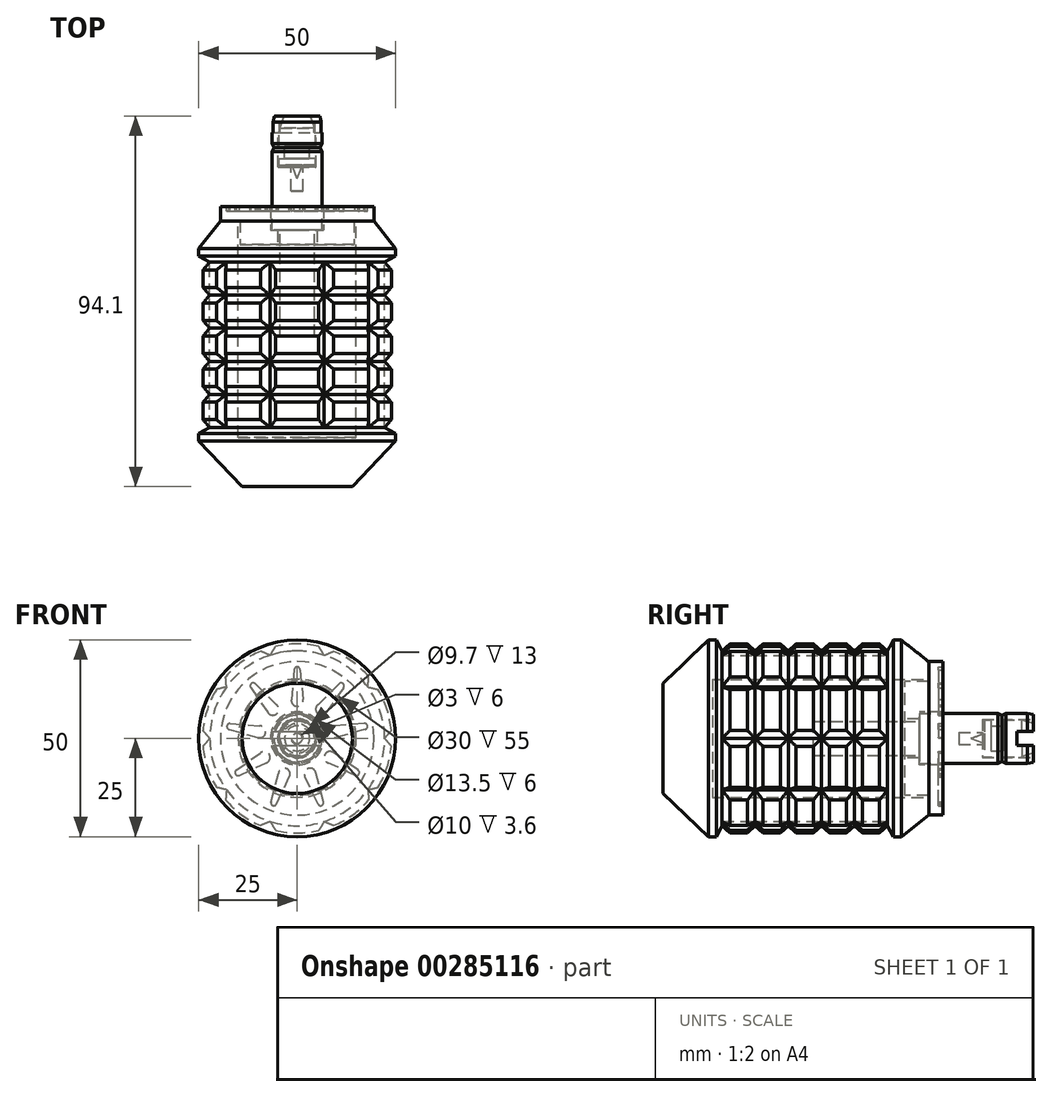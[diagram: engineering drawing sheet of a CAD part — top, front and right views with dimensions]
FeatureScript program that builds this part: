
annotation { "Feature Type Name" : "Feature", "Feature Type Description" : "" }
export const myFeature = defineFeature(function(context is Context, id is Id, definition is map)
    precondition{}
    {
        {
            var Q0;
            Q0=qCreatedBy(makeId("Front.planeOp"),FACE);
            var sketch = newSketch(context, id + "F0", { "sketchPlane" : qUnion([Q0])});
            skArc(sketch, "E0", {"start": v(-9.3, 22.13) * mm, "mid": v(-14.1, 19.42) * mm, "end": v(-18.17, 15.67) * mm});
            skLineSegment(sketch, "E1", {"start": v(-9.3, 22.13) * mm, "end": v(-6.86, 21.11) * mm});
            skLineSegment(sketch, "E2", {"start": v(-5.5, 23.36) * mm, "end": v(-6.86, 21.11) * mm});
            skLineSegment(sketch, "E3.1.0", {"start": v(-18.17, 15.67) * mm, "end": v(-17.96, 13.05) * mm});
            skLineSegment(sketch, "E3.1.1", {"start": v(-20.52, 12.44) * mm, "end": v(-17.96, 13.05) * mm});
            skLineSegment(sketch, "E3.2.0", {"start": v(-23.92, 2) * mm, "end": v(-22.2, 0) * mm});
            skLineSegment(sketch, "E3.2.1", {"start": v(-23.92, -2) * mm, "end": v(-22.2, 0) * mm});
            skLineSegment(sketch, "E3.3.0", {"start": v(-20.52, -12.44) * mm, "end": v(-17.96, -13.05) * mm});
            skLineSegment(sketch, "E3.3.1", {"start": v(-18.17, -15.67) * mm, "end": v(-17.96, -13.05) * mm});
            skLineSegment(sketch, "E3.4.0", {"start": v(-9.3, -22.13) * mm, "end": v(-6.86, -21.11) * mm});
            skLineSegment(sketch, "E3.4.1", {"start": v(-5.5, -23.36) * mm, "end": v(-6.86, -21.11) * mm});
            skLineSegment(sketch, "E3.5.0", {"start": v(5.5, -23.36) * mm, "end": v(6.86, -21.11) * mm});
            skLineSegment(sketch, "E3.5.1", {"start": v(9.3, -22.13) * mm, "end": v(6.86, -21.11) * mm});
            skLineSegment(sketch, "E3.6.0", {"start": v(18.17, -15.67) * mm, "end": v(17.96, -13.05) * mm});
            skLineSegment(sketch, "E3.6.1", {"start": v(20.52, -12.44) * mm, "end": v(17.96, -13.05) * mm});
            skLineSegment(sketch, "E3.7.0", {"start": v(23.92, -2) * mm, "end": v(22.2, 0) * mm});
            skLineSegment(sketch, "E3.7.1", {"start": v(23.92, 2) * mm, "end": v(22.2, 0) * mm});
            skLineSegment(sketch, "E3.8.0", {"start": v(20.52, 12.44) * mm, "end": v(17.96, 13.05) * mm});
            skLineSegment(sketch, "E3.8.1", {"start": v(18.17, 15.67) * mm, "end": v(17.96, 13.05) * mm});
            skLineSegment(sketch, "E3.9.0", {"start": v(9.3, 22.13) * mm, "end": v(6.86, 21.11) * mm});
            skLineSegment(sketch, "E3.9.1", {"start": v(5.5, 23.36) * mm, "end": v(6.86, 21.11) * mm});
            skArc(sketch, "E4.trimOffspring", {"start": v(-20.52, 12.44) * mm, "mid": v(-22.83, 7.42) * mm, "end": v(-23.92, 2) * mm});
            skArc(sketch, "E5.trimOffspring", {"start": v(-23.92, -2) * mm, "mid": v(-22.83, -7.42) * mm, "end": v(-20.52, -12.44) * mm});
            skArc(sketch, "E6.trimOffspring", {"start": v(-18.17, -15.67) * mm, "mid": v(-14.1, -19.42) * mm, "end": v(-9.3, -22.13) * mm});
            skArc(sketch, "E7.trimOffspring", {"start": v(23.92, 2) * mm, "mid": v(22.83, 7.42) * mm, "end": v(20.52, 12.44) * mm});
            skArc(sketch, "E8.trimOffspring", {"start": v(20.52, -12.44) * mm, "mid": v(22.83, -7.42) * mm, "end": v(23.92, -2) * mm});
            skArc(sketch, "E9.trimOffspring", {"start": v(9.3, -22.13) * mm, "mid": v(14.1, -19.42) * mm, "end": v(18.17, -15.67) * mm});
            skArc(sketch, "E10.trimOffspring", {"start": v(-5.5, -23.36) * mm, "mid": v(0, -24) * mm, "end": v(5.5, -23.36) * mm});
            skArc(sketch, "E11.trimOffspring", {"start": v(18.17, 15.67) * mm, "mid": v(14.1, 19.42) * mm, "end": v(9.3, 22.13) * mm});
            skArc(sketch, "E12.trimOffspring", {"start": v(5.5, 23.36) * mm, "mid": v(0, 24) * mm, "end": v(-5.5, 23.36) * mm});
            skSolve(sketch);
        }
        {
            var Q0;
            Q0 = qSketchRegion(id + "F0", true);
            extrude(context, id + "F1", {"entities" : qUnion([Q0]), "endBound" : BoundingType.SYMMETRIC, "depth" : 42 * mm});
        }
        {
            var Q0;
            Q0=qCreatedBy(makeId("Right.planeOp"),FACE);
            var sketch = newSketch(context, id + "F2", { "sketchPlane" : qUnion([Q0])});
            skLineSegment(sketch, "E13.0", {"start": v(21, 23.36) * mm, "end": v(21, 24) * mm, "construction": true});
            skLineSegment(sketch, "E14.0", {"start": v(21, 23.36) * mm, "end": v(21, 21.11) * mm, "construction": true});
            skLineSegment(sketch, "E15", {"start": v(0, 0) * mm, "end": v(0, 30.64) * mm, "construction": true});
            skLineSegment(sketch, "E16", {"start": v(21, 24.46) * mm, "end": v(21, 27.24) * mm, "construction": true});
            skLineSegment(sketch, "E17", {"start": v(21, 27.24) * mm, "end": v(-21, 27.24) * mm, "construction": true});
            skLineSegment(sketch, "E18", {"start": v(-21, 27.24) * mm, "end": v(-21, 24) * mm, "construction": true});
            skPoint(sketch, "E19.0.end.orphan", {"position": v(-21, 21.11) * mm});
            skLineSegment(sketch, "E20", {"start": v(-21, 24) * mm, "end": v(-21, 22.2) * mm});
            skPoint(sketch, "E21.end.orphan", {"position": v(21, 24) * mm});
            skLineSegment(sketch, "E22", {"start": v(-19, 24) * mm, "end": v(-21, 22.2) * mm});
            skLineSegment(sketch, "E23", {"start": v(-21, 27.24) * mm, "end": v(-12.6, 27.24) * mm});
            skLineSegment(sketch, "E24", {"start": v(-12.6, 27.24) * mm, "end": v(-4.2, 27.24) * mm});
            skLineSegment(sketch, "E25", {"start": v(-4.2, 27.24) * mm, "end": v(4.2, 27.24) * mm});
            skLineSegment(sketch, "E26", {"start": v(4.2, 27.24) * mm, "end": v(12.6, 27.24) * mm});
            skLineSegment(sketch, "E27", {"start": v(12.6, 27.24) * mm, "end": v(21, 27.24) * mm});
            skLineSegment(sketch, "E28", {"start": v(-12.6, 27.24) * mm, "end": v(-12.6, 10.8) * mm, "construction": true});
            skLineSegment(sketch, "E29", {"start": v(-4.2, 27.24) * mm, "end": v(-4.2, 11.63) * mm, "construction": true});
            skLineSegment(sketch, "E30", {"start": v(4.2, 27.24) * mm, "end": v(4.2, 11.59) * mm, "construction": true});
            skLineSegment(sketch, "E31", {"start": v(12.6, 27.24) * mm, "end": v(12.6, 11.39) * mm, "construction": true});
            skLineSegment(sketch, "E32", {"start": v(-19, 24) * mm, "end": v(-14.6, 24) * mm});
            skPoint(sketch, "E33", {"position": v(-12.6, 24) * mm});
            skPoint(sketch, "E34", {"position": v(-4.2, 24) * mm});
            skPoint(sketch, "E35", {"position": v(4.2, 24) * mm});
            skPoint(sketch, "E36", {"position": v(12.6, 24) * mm});
            skLineSegment(sketch, "E37", {"start": v(-12.6, 22.2) * mm, "end": v(-14.6, 24) * mm});
            skLineSegment(sketch, "E38", {"start": v(-10.6, 24) * mm, "end": v(-12.6, 22.2) * mm});
            skLineSegment(sketch, "E39", {"start": v(-6.2, 24) * mm, "end": v(-4.2, 22.2) * mm});
            skLineSegment(sketch, "E40", {"start": v(-4.2, 22.2) * mm, "end": v(-2.2, 24) * mm});
            skLineSegment(sketch, "E41", {"start": v(2.2, 24) * mm, "end": v(4.2, 22.2) * mm});
            skLineSegment(sketch, "E42", {"start": v(4.2, 22.2) * mm, "end": v(6.2, 24) * mm});
            skLineSegment(sketch, "E43", {"start": v(10.6, 24) * mm, "end": v(12.6, 22.2) * mm});
            skLineSegment(sketch, "E44", {"start": v(12.6, 22.2) * mm, "end": v(14.6, 24) * mm});
            skLineSegment(sketch, "E45", {"start": v(21, 22.2) * mm, "end": v(19, 24) * mm});
            skLineSegment(sketch, "E46", {"start": v(-21, 27.24) * mm, "end": v(-21, 22.2) * mm});
            skLineSegment(sketch, "E47", {"start": v(21, 27.24) * mm, "end": v(21, 22.2) * mm});
            skLineSegment(sketch, "E48.trimOffspring", {"start": v(-10.6, 24) * mm, "end": v(-6.2, 24) * mm});
            skLineSegment(sketch, "E49.trimOffspring", {"start": v(-2.2, 24) * mm, "end": v(2.2, 24) * mm});
            skLineSegment(sketch, "E50.trimOffspring", {"start": v(6.2, 24) * mm, "end": v(10.6, 24) * mm});
            skLineSegment(sketch, "E51.trimOffspring", {"start": v(14.6, 24) * mm, "end": v(19, 24) * mm});
            skLineSegment(sketch, "E52", {"start": v(0, 0) * mm, "end": v(61.19, 0) * mm, "construction": true});
            skLineSegment(sketch, "E53", {"start": v(0, 0) * mm, "end": v(-52.13, 0) * mm, "construction": true});
            skSolve(sketch);
        }
        {
            var Q0;
            Q0 = qSketchRegion(id + "F2", true);
            var Q1;
            Q1=sQuery(id+"F2.wireOp",EDGE,"E52");
            revolve(context, id + "F3", {"operationType" : NewBodyOperationType.REMOVE, "entities" : qUnion([Q0]), "axis" : qUnion([Q1]), "revolveType" : RevolveType.FULL, "oppositeDirection" : true});
        }
        {
            var Q0;
            Q0=qCreatedBy(makeId("Top.planeOp"),FACE);
            var sketch = newSketch(context, id + "F4", { "sketchPlane" : qUnion([Q0])});
            skLineSegment(sketch, "E54", {"start": v(0, 0) * mm, "end": v(0, 21) * mm, "construction": true});
            skLineSegment(sketch, "E55", {"start": v(0, 0) * mm, "end": v(0, -40.18) * mm, "construction": true});
            skPoint(sketch, "E56.0", {"position": v(-22.2, 21) * mm});
            skPoint(sketch, "E57", {"position": v(0, 21) * mm});
            skPoint(sketch, "E58.orphan", {"position": v(6.86, 21) * mm});
            skPoint(sketch, "E59.trimOffspring.end.orphan", {"position": v(22.2, 21) * mm});
            skPoint(sketch, "E59.trimOffspring.start.orphan", {"position": v(17.96, 21) * mm});
            skLineSegment(sketch, "E60", {"start": v(-25, 24.5) * mm, "end": v(-25, 22.5) * mm});
            skLineSegment(sketch, "E61", {"start": v(-19.5, 31.5) * mm, "end": v(-25, 24.5) * mm});
            skLineSegment(sketch, "E62", {"start": v(-25, 24.5) * mm, "end": v(-25, 22.5) * mm, "construction": true});
            skLineSegment(sketch, "E63", {"start": v(-25, 22.5) * mm, "end": v(-22.2, 21) * mm});
            skPoint(sketch, "E64.0.start.orphan", {"position": v(-17.96, 21) * mm});
            skPoint(sketch, "E65.0.start.orphan", {"position": v(-6.86, 21) * mm});
            skLineSegment(sketch, "E66.trimOffspring", {"start": v(0, 31.5) * mm, "end": v(0, 57.57) * mm, "construction": true});
            skLineSegment(sketch, "E67", {"start": v(0, 31.5) * mm, "end": v(-19.5, 31.5) * mm});
            skLineSegment(sketch, "E68", {"start": v(0, 31.5) * mm, "end": v(0, 21) * mm});
            skLineSegment(sketch, "E69", {"start": v(-22.2, 21) * mm, "end": v(0, 21) * mm});
            skLineSegment(sketch, "E70", {"start": v(0, 35.81) * mm, "end": v(0, 0) * mm, "construction": true});
            skLineSegment(sketch, "E71.MirrorCS", {"start": v(-25, -22.5) * mm, "end": v(-22.2, -21) * mm});
            skLineSegment(sketch, "E72.MirrorCS", {"start": v(-22.2, -21) * mm, "end": v(0, -21) * mm});
            skLineSegment(sketch, "E73", {"start": v(0, -21) * mm, "end": v(0, -36) * mm});
            skLineSegment(sketch, "E74", {"start": v(0, -36) * mm, "end": v(-14, -36) * mm});
            skPoint(sketch, "E75.MirrorCS.end.orphan", {"position": v(-25, -22.5) * mm});
            skPoint(sketch, "E75.MirrorCS.start.orphan", {"position": v(-25, -24.5) * mm});
            skLineSegment(sketch, "E76", {"start": v(-25, -22.5) * mm, "end": v(-25, -24.5) * mm});
            skPoint(sketch, "E77.MirrorCS.start.orphan", {"position": v(0, -31.5) * mm});
            skLineSegment(sketch, "E78", {"start": v(-25, -24.5) * mm, "end": v(-14, -36) * mm});
            skSolve(sketch);
        }
        {
            var Q0;
            Q0 = qSketchRegion(id + "F4", true);
            var Q1;
            Q1=sQuery(id+"F4.wireOp",EDGE,"E68");
            revolve(context, id + "F5", {"operationType" : NewBodyOperationType.ADD, "entities" : qUnion([Q0]), "axis" : qUnion([Q1]), "revolveType" : RevolveType.FULL});
        }
        {
            var Q0;
            Q0=makeQuery(id+"F5.opRevolve","SWEPT_FACE",FACE,{"disambiguationData":[OSD([sQuery(id+"F4.wireOp",EDGE,"E67")])]});
            cPlane(context, id + "F6", {"entities" : qUnion([Q0]), "cplaneType" : CPlaneType.OFFSET, "offset" : 0 * mm, "width" : 150 * mm, "height" : 150 * mm});
        }
        {
            var Q0;
            Q0=qCreatedBy(id+"F6.planeOp",FACE);
            var sketch = newSketch(context, id + "F7", { "sketchPlane" : qUnion([Q0])});
            skCircle(sketch, "E79", {"center": v(0, 0) * mm, "radius": 15 * mm});
            skSolve(sketch);
        }
        {
            var Q0;
            Q0 = qSketchRegion(id + "F7", true);
            extrude(context, id + "F8", {"entities" : qUnion([Q0]), "operationType" : NewBodyOperationType.REMOVE, "oppositeDirection" : true, "depth" : 55 * mm});
        }
        {
            var Q0;
            Q0=qCreatedBy(makeId("Top.planeOp"),FACE);
            var sketch = newSketch(context, id + "F9", { "sketchPlane" : qUnion([Q0])});
            skLineSegment(sketch, "E80", {"start": v(0, 0) * mm, "end": v(0, 31.5) * mm, "construction": true});
            skLineSegment(sketch, "E81.0", {"start": v(-15, 31.5) * mm, "end": v(0, 31.5) * mm, "construction": true});
            skLineSegment(sketch, "E82.0", {"start": v(-19.5, 31.5) * mm, "end": v(0, 31.5) * mm, "construction": true});
            skPoint(sketch, "E83", {"position": v(0, 31.5) * mm});
            skLineSegment(sketch, "E84", {"start": v(14.5, 31.5) * mm, "end": v(14.5, 25.5) * mm});
            skLineSegment(sketch, "E85.trimOffspring", {"start": v(14.5, 31.5) * mm, "end": v(19.5, 31.5) * mm, "construction": true});
            skLineSegment(sketch, "E86.trimOffspring", {"start": v(14.5, 31.5) * mm, "end": v(15, 31.5) * mm, "construction": true});
            skLineSegment(sketch, "E87", {"start": v(5, 25.5) * mm, "end": v(14.5, 25.5) * mm});
            skLineSegment(sketch, "E88", {"start": v(19.5, 31.5) * mm, "end": v(19.5, 35.1) * mm});
            skLineSegment(sketch, "E89", {"start": v(19.5, 35.1) * mm, "end": v(6.75, 35.1) * mm});
            skLineSegment(sketch, "E90", {"start": v(0, 31.5) * mm, "end": v(0, 25.5) * mm});
            skLineSegment(sketch, "E91", {"start": v(14.5, 31.5) * mm, "end": v(19.5, 31.5) * mm});
            skLineSegment(sketch, "E92", {"start": v(6.75, 35.1) * mm, "end": v(6.75, 29.1) * mm});
            skLineSegment(sketch, "E93", {"start": v(6.75, 29.1) * mm, "end": v(5, 29.1) * mm});
            skLineSegment(sketch, "E94", {"start": v(5, 25.5) * mm, "end": v(5, 29.1) * mm});
            skLineSegment(sketch, "E95.trimOffspring", {"start": v(0, 35.1) * mm, "end": v(0, 71.87) * mm, "construction": true});
            skSolve(sketch);
        }
        {
            var Q0;
            Q0 = qSketchRegion(id + "F9", true);
            var Q1;
            Q1=sQuery(id+"F9.wireOp",EDGE,"E95.trimOffspring");
            revolve(context, id + "F10", {"entities" : qUnion([Q0]), "axis" : qUnion([Q1]), "revolveType" : RevolveType.FULL});
        }
        {
            var Q0;
            Q0=makeQuery(id+"F10.opRevolve","SWEPT_FACE",FACE,{"disambiguationData":[OSD([sQuery(id+"F9.wireOp",EDGE,"E89")])]});
            cPlane(context, id + "F11", {"entities" : qUnion([Q0]), "cplaneType" : CPlaneType.OFFSET, "offset" : 0 * mm, "width" : 150 * mm, "height" : 150 * mm});
        }
        {
            var Q0;
            Q0=qCreatedBy(id+"F11.planeOp",FACE);
            var sketch = newSketch(context, id + "F12", { "sketchPlane" : qUnion([Q0])});
            skCircle(sketch, "E96.0.0", {"center": v(0, 0) * mm, "radius": 19.5 * mm, "construction": true});
            skLineSegment(sketch, "E97", {"start": v(-32.31, 0) * mm, "end": v(39.47, 0) * mm, "construction": true});
            skLineSegment(sketch, "E98", {"start": v(0, 28.13) * mm, "end": v(0, 18.15) * mm, "construction": true});
            skPoint(sketch, "E99", {"position": v(0, 8.15) * mm});
            skArc(sketch, "E100", {"start": v(-1.47, 9.94) * mm, "mid": v(0, 8.15) * mm, "end": v(1.47, 9.94) * mm});
            skArc(sketch, "E101", {"start": v(0.75, 17.4) * mm, "mid": v(0, 18.15) * mm, "end": v(-0.75, 17.4) * mm});
            skLineSegment(sketch, "E102", {"start": v(-0.75, 17.4) * mm, "end": v(-1.5, 9.65) * mm});
            skLineSegment(sketch, "E103", {"start": v(0.75, 17.4) * mm, "end": v(1.5, 9.65) * mm});
            skLineSegment(sketch, "E104.trimOffspring", {"start": v(0, 8.15) * mm, "end": v(0, -29.51) * mm, "construction": true});
            skArc(sketch, "E105.1.0", {"start": v(11.76, 12.85) * mm, "mid": v(11.67, 13.9) * mm, "end": v(10.6, 13.81) * mm});
            skLineSegment(sketch, "E105.1.1", {"start": v(11.76, 12.85) * mm, "end": v(7.35, 6.43) * mm});
            skArc(sketch, "E105.1.2", {"start": v(5.26, 8.56) * mm, "mid": v(5.24, 6.24) * mm, "end": v(7.52, 6.67) * mm});
            skLineSegment(sketch, "E105.1.3", {"start": v(10.6, 13.81) * mm, "end": v(5.05, 8.36) * mm});
            skArc(sketch, "E105.2.0", {"start": v(17.27, 2.28) * mm, "mid": v(17.87, 3.15) * mm, "end": v(17, 3.76) * mm});
            skLineSegment(sketch, "E105.2.1", {"start": v(17.27, 2.28) * mm, "end": v(9.76, 0.2) * mm});
            skArc(sketch, "E105.2.2", {"start": v(9.53, 3.18) * mm, "mid": v(8.03, 1.42) * mm, "end": v(10.04, 0.28) * mm});
            skLineSegment(sketch, "E105.2.3", {"start": v(17, 3.76) * mm, "end": v(9.24, 3.15) * mm});
            skArc(sketch, "E105.3.0", {"start": v(14.7, -9.35) * mm, "mid": v(15.72, -9.08) * mm, "end": v(15.44, -8.05) * mm});
            skLineSegment(sketch, "E105.3.1", {"start": v(14.7, -9.35) * mm, "end": v(7.6, -6.12) * mm});
            skArc(sketch, "E105.3.2", {"start": v(9.34, -3.7) * mm, "mid": v(7.06, -4.08) * mm, "end": v(7.87, -6.24) * mm});
            skLineSegment(sketch, "E105.3.3", {"start": v(15.44, -8.05) * mm, "end": v(9.1, -3.53) * mm});
            skArc(sketch, "E105.4.0", {"start": v(5.25, -16.6) * mm, "mid": v(6.2, -17.06) * mm, "end": v(6.66, -16.1) * mm});
            skLineSegment(sketch, "E105.4.1", {"start": v(5.25, -16.6) * mm, "end": v(1.9, -9.58) * mm});
            skArc(sketch, "E105.4.2", {"start": v(4.78, -8.83) * mm, "mid": v(2.79, -7.66) * mm, "end": v(2.02, -9.84) * mm});
            skLineSegment(sketch, "E105.4.3", {"start": v(6.66, -16.1) * mm, "end": v(4.71, -8.56) * mm});
            skArc(sketch, "E105.5.0", {"start": v(-6.66, -16.1) * mm, "mid": v(-6.2, -17.06) * mm, "end": v(-5.25, -16.6) * mm});
            skLineSegment(sketch, "E105.5.1", {"start": v(-6.66, -16.1) * mm, "end": v(-4.71, -8.56) * mm});
            skArc(sketch, "E105.5.2", {"start": v(-2.02, -9.84) * mm, "mid": v(-2.79, -7.66) * mm, "end": v(-4.78, -8.83) * mm});
            skLineSegment(sketch, "E105.5.3", {"start": v(-5.25, -16.6) * mm, "end": v(-1.9, -9.58) * mm});
            skArc(sketch, "E105.6.0", {"start": v(-15.44, -8.05) * mm, "mid": v(-15.72, -9.07) * mm, "end": v(-14.7, -9.35) * mm});
            skLineSegment(sketch, "E105.6.1", {"start": v(-15.44, -8.05) * mm, "end": v(-9.1, -3.53) * mm});
            skArc(sketch, "E105.6.2", {"start": v(-7.87, -6.24) * mm, "mid": v(-7.06, -4.07) * mm, "end": v(-9.34, -3.7) * mm});
            skLineSegment(sketch, "E105.6.3", {"start": v(-14.7, -9.35) * mm, "end": v(-7.6, -6.12) * mm});
            skArc(sketch, "E105.7.0", {"start": v(-17, 3.76) * mm, "mid": v(-17.87, 3.15) * mm, "end": v(-17.27, 2.28) * mm});
            skLineSegment(sketch, "E105.7.1", {"start": v(-17, 3.76) * mm, "end": v(-9.24, 3.15) * mm});
            skArc(sketch, "E105.7.2", {"start": v(-10.04, 0.28) * mm, "mid": v(-8.03, 1.42) * mm, "end": v(-9.53, 3.18) * mm});
            skLineSegment(sketch, "E105.7.3", {"start": v(-17.27, 2.28) * mm, "end": v(-9.76, 0.2) * mm});
            skArc(sketch, "E105.8.0", {"start": v(-10.6, 13.81) * mm, "mid": v(-11.67, 13.9) * mm, "end": v(-11.76, 12.85) * mm});
            skLineSegment(sketch, "E105.8.1", {"start": v(-10.6, 13.81) * mm, "end": v(-5.05, 8.36) * mm});
            skArc(sketch, "E105.8.2", {"start": v(-7.52, 6.67) * mm, "mid": v(-5.24, 6.24) * mm, "end": v(-5.26, 8.56) * mm});
            skLineSegment(sketch, "E105.8.3", {"start": v(-11.76, 12.85) * mm, "end": v(-7.35, 6.43) * mm});
            skLineSegment(sketch, "E105.anchor1", {"start": v(0, 0) * mm, "end": v(-0.75, 17.4) * mm, "construction": true});
            skLineSegment(sketch, "E105.anchor2", {"start": v(0, 0) * mm, "end": v(-0.75, 17.4) * mm, "construction": true});
            skSolve(sketch);
        }
        {
            var Q0;
            Q0 = qSketchRegion(id + "F12", true);
            extrude(context, id + "F13", {"entities" : qUnion([Q0]), "operationType" : NewBodyOperationType.REMOVE, "oppositeDirection" : true, "depth" : 1.1 * mm});
        }
        {
            var Q0;
            Q0=qCreatedBy(makeId("Right.planeOp"),FACE);
            var sketch = newSketch(context, id + "F14", { "sketchPlane" : qUnion([Q0])});
            skLineSegment(sketch, "E106", {"start": v(59.1, 0) * mm, "end": v(45.1, 0) * mm, "construction": true});
            skLineSegment(sketch, "E107", {"start": v(0, -67.3) * mm, "end": v(0, 60.31) * mm, "construction": true});
            skLineSegment(sketch, "E108.0", {"start": v(29.1, -6.75) * mm, "end": v(29.1, 6.75) * mm, "construction": true});
            skLineSegment(sketch, "E109.0", {"start": v(25.5, -5) * mm, "end": v(25.5, -4.35) * mm, "construction": true});
            skLineSegment(sketch, "E110.0", {"start": v(35.1, -6.75) * mm, "end": v(35.1, 6.75) * mm, "construction": true});
            skLineSegment(sketch, "E111", {"start": v(25.5, -5) * mm, "end": v(29.1, -5) * mm, "construction": true});
            skLineSegment(sketch, "E112", {"start": v(29.1, -6.75) * mm, "end": v(35.1, -6.75) * mm, "construction": true});
            skLineSegment(sketch, "E113", {"start": v(29.1, -6.75) * mm, "end": v(29.1, 0) * mm, "construction": true});
            skLineSegment(sketch, "E114", {"start": v(25.5, -5) * mm, "end": v(25.5, -4.35) * mm});
            skLineSegment(sketch, "E115", {"start": v(35.1, -6.75) * mm, "end": v(35.1, 0) * mm});
            skLineSegment(sketch, "E116", {"start": v(2.1, 0) * mm, "end": v(2.1, -4.35) * mm});
            skLineSegment(sketch, "E117", {"start": v(2.1, -4.35) * mm, "end": v(29.1, -4.35) * mm});
            skLineSegment(sketch, "E118", {"start": v(58.1, 0) * mm, "end": v(58.1, -6.05) * mm});
            skLineSegment(sketch, "E119", {"start": v(56.6, -6.35) * mm, "end": v(51.1, -6.35) * mm});
            skLineSegment(sketch, "E120", {"start": v(29.1, -6.35) * mm, "end": v(29.1, -4.35) * mm});
            skLineSegment(sketch, "E121", {"start": v(58.1, -4.85) * mm, "end": v(45.1, -4.85) * mm});
            skLineSegment(sketch, "E122", {"start": v(45.1, -4.85) * mm, "end": v(45.1, -1.5) * mm});
            skLineSegment(sketch, "E123", {"start": v(39.1, 0) * mm, "end": v(2.1, 0) * mm});
            skLineSegment(sketch, "E124", {"start": v(50.1, -5.87) * mm, "end": v(50.1, -4.85) * mm});
            skLineSegment(sketch, "E125", {"start": v(50.1, -5.87) * mm, "end": v(49.1, -6.35) * mm});
            skLineSegment(sketch, "E126", {"start": v(50.1, -5.87) * mm, "end": v(51.1, -6.35) * mm});
            skLineSegment(sketch, "E127", {"start": v(58.1, -6.05) * mm, "end": v(56.6, -6.35) * mm});
            skPoint(sketch, "E128.orphan", {"position": v(58.1, -6.35) * mm});
            skLineSegment(sketch, "E129.trimOffspring", {"start": v(49.1, -6.35) * mm, "end": v(29.1, -6.35) * mm});
            skPoint(sketch, "E130.orphan", {"position": v(50.1, -6.35) * mm});
            skLineSegment(sketch, "E131.trimOffspring", {"start": v(25.5, 0) * mm, "end": v(25.5, 5) * mm, "construction": true});
            skLineSegment(sketch, "E132", {"start": v(45.1, -1.5) * mm, "end": v(39.1, -1.5) * mm});
            skLineSegment(sketch, "E133", {"start": v(39.1, -1.5) * mm, "end": v(39.1, 0) * mm});
            skLineSegment(sketch, "E134.trimOffspring", {"start": v(39.1, 0) * mm, "end": v(-46.03, 0) * mm, "construction": true});
            skSolve(sketch);
        }
        {
            var Q0;
            Q0 = qSketchRegion(id + "F14", true);
            var Q1;
            Q1=sQuery(id+"F14.wireOp",EDGE,"E106");
            revolve(context, id + "F15", {"entities" : qUnion([Q0]), "axis" : qUnion([Q1]), "revolveType" : RevolveType.FULL});
        }
        {
            var Q0;
            Q0=qCreatedBy(makeId("Right.planeOp"),FACE);
            var sketch = newSketch(context, id + "F16", { "sketchPlane" : qUnion([Q0])});
            skLineSegment(sketch, "E135", {"start": v(58.1, -4.85) * mm, "end": v(45.1, -4.85) * mm, "construction": true});
            skLineSegment(sketch, "E136.0", {"start": v(58.1, 6.05) * mm, "end": v(58.1, 4.85) * mm, "construction": true});
            skLineSegment(sketch, "E137.0", {"start": v(58.1, -4.65) * mm, "end": v(58.1, -4.85) * mm, "construction": true});
            skLineSegment(sketch, "E138.0", {"start": v(45.1, 4.85) * mm, "end": v(45.1, -4.85) * mm, "construction": true});
            skLineSegment(sketch, "E139", {"start": v(45.1, -1.5) * mm, "end": v(39.1, -1.5) * mm, "construction": true});
            skLineSegment(sketch, "E140", {"start": v(39.1, 1.5) * mm, "end": v(45.1, 1.5) * mm, "construction": true});
            skLineSegment(sketch, "E141", {"start": v(68.4, 0) * mm, "end": v(-18.4, 0) * mm, "construction": true});
            skPoint(sketch, "E141.endSnap0", {"position": v(45.1, 0) * mm});
            skPoint(sketch, "E142", {"position": v(58.1, 0) * mm});
            skPoint(sketch, "E143", {"position": v(42.33, 0) * mm});
            skLineSegment(sketch, "E144", {"start": v(45.1, 0) * mm, "end": v(45.6, 0) * mm, "construction": true});
            skLineSegment(sketch, "E145", {"start": v(45.1, -4.85) * mm, "end": v(45.1, -4.65) * mm, "construction": true});
            skLineSegment(sketch, "E146", {"start": v(45.6, -1.28) * mm, "end": v(45.6, -4.65) * mm});
            skLineSegment(sketch, "E147", {"start": v(45.6, -4.65) * mm, "end": v(47.31, -4.65) * mm});
            skPoint(sketch, "E148.orphan", {"position": v(58.1, -6.05) * mm});
            skPoint(sketch, "E149.orphan", {"position": v(58.1, 4.85) * mm});
            skLineSegment(sketch, "E150.trimOffspring", {"start": v(58.1, 0) * mm, "end": v(58.1, -3.75) * mm, "construction": true});
            skLineSegment(sketch, "E151", {"start": v(45.6, -4.65) * mm, "end": v(47.3, -4.65) * mm, "construction": true});
            skLineSegment(sketch, "E152", {"start": v(47.31, -4.67) * mm, "end": v(47.31, -3.17) * mm});
            skLineSegment(sketch, "E153", {"start": v(47.31, -3.17) * mm, "end": v(50.31, -3.17) * mm});
            skLineSegment(sketch, "E154", {"start": v(50.31, -3.17) * mm, "end": v(50.31, -4.65) * mm});
            skLineSegment(sketch, "E155", {"start": v(50.31, -4.65) * mm, "end": v(55.11, -4.65) * mm, "construction": true});
            skLineSegment(sketch, "E156", {"start": v(58.1, -3.75) * mm, "end": v(58.1, -3.05) * mm, "construction": true});
            skLineSegment(sketch, "E157", {"start": v(58.1, -3.75) * mm, "end": v(58.1, -1.75) * mm, "construction": true});
            skLineSegment(sketch, "E158", {"start": v(58.1, -1.75) * mm, "end": v(58.1, -3.75) * mm});
            skLineSegment(sketch, "E159", {"start": v(58.1, -1.75) * mm, "end": v(53.9, -1.75) * mm});
            skLineSegment(sketch, "E160", {"start": v(53.9, -1.75) * mm, "end": v(53.9, 0) * mm});
            skLineSegment(sketch, "E161", {"start": v(53.9, 0) * mm, "end": v(45.6, 0) * mm});
            skLineSegment(sketch, "E162", {"start": v(59.64, 0) * mm, "end": v(59.64, -3.75) * mm, "construction": true});
            skLineSegment(sketch, "E163", {"start": v(59.64, -3.75) * mm, "end": v(58.1, -3.75) * mm, "construction": true});
            skLineSegment(sketch, "E164", {"start": v(58.1, -3.75) * mm, "end": v(55.11, -4.65) * mm});
            skLineSegment(sketch, "E165.trimOffspring", {"start": v(50.31, -4.65) * mm, "end": v(55.11, -4.65) * mm});
            skLineSegment(sketch, "E166", {"start": v(45.1, -1.5) * mm, "end": v(45.6, -1.5) * mm, "construction": true});
            skLineSegment(sketch, "E167", {"start": v(44.75, -1.5) * mm, "end": v(44.75, -1.28) * mm, "construction": true});
            skLineSegment(sketch, "E168", {"start": v(44.75, -1.28) * mm, "end": v(45.1, -1.28) * mm, "construction": true});
            skLineSegment(sketch, "E169", {"start": v(45.6, -1.28) * mm, "end": v(42.24, 0) * mm});
            skLineSegment(sketch, "E170", {"start": v(42.24, 0) * mm, "end": v(45.6, 0) * mm});
            skSolve(sketch);
        }
        {
            var Q0;
            Q0 = qSketchRegion(id + "F16", true);
            var Q1;
            Q1=sQuery(id+"F16.wireOp",EDGE,"E141");
            revolve(context, id + "F17", {"entities" : qUnion([Q0]), "axis" : qUnion([Q1]), "revolveType" : RevolveType.FULL});
        }
        {
            var Q0;
            Q0=qCreatedBy(makeId("Right.planeOp"),FACE);
            var sketch = newSketch(context, id + "F18", { "sketchPlane" : qUnion([Q0])});
            skLineSegment(sketch, "E171", {"start": v(58.1, -1.75) * mm, "end": v(53.9, -1.75) * mm, "construction": true});
            skLineSegment(sketch, "E172", {"start": v(53.9, 1.75) * mm, "end": v(58.1, 1.75) * mm, "construction": true});
            skLineSegment(sketch, "E173", {"start": v(53.9, -1.75) * mm, "end": v(53.9, 1.75) * mm});
            skLineSegment(sketch, "E174", {"start": v(53.9, 1.75) * mm, "end": v(58.1, 1.75) * mm});
            skLineSegment(sketch, "E175", {"start": v(61.04, 1.75) * mm, "end": v(61.04, -1.75) * mm});
            skLineSegment(sketch, "E176", {"start": v(61.04, -1.75) * mm, "end": v(53.58, -1.75) * mm});
            skLineSegment(sketch, "E177", {"start": v(61.04, 1.75) * mm, "end": v(53.9, 1.75) * mm});
            skSolve(sketch);
        }
        {
            var Q0;
            Q0 = qSketchRegion(id + "F18", true);
            extrude(context, id + "F19", {"entities" : qUnion([Q0]), "operationType" : NewBodyOperationType.REMOVE, "endBound" : BoundingType.SYMMETRIC, "oppositeDirection" : true, "depth" : 25 * mm});
        }
    });
